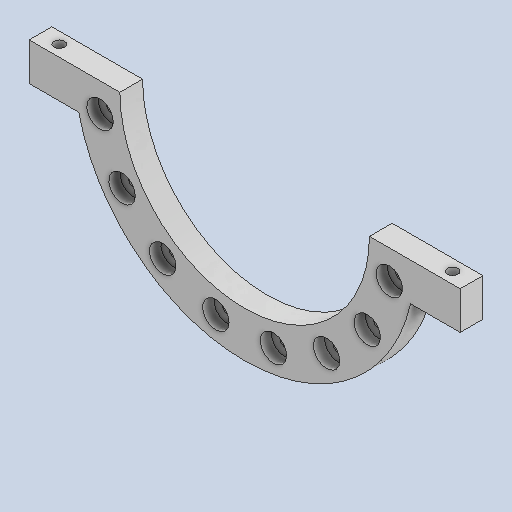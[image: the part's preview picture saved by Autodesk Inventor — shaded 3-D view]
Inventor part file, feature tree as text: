
AUTODESK INVENTOR PART (.ipt)
format: ipt  version: 2025 (Build 290162010, 162A)  size: 263,680 bytes
history: native  units: mm
features: extrude x4, sketch x4, other x2, pattern_circular x1, mirror x1
ambient origin geometry x8: Origin, YZ Plane, XZ Plane, XY Plane, X Axis, Y Axis, Z Axis, Center Point
bodies: Solid1 (feature_tree)
feature tree (12):
  extrude  "Extrusion1"  Depth=30.0mm
  extrude  "Extrusion4"  TaperAngle=0.0deg  [1 undecoded]
  extrude  "Extrusion5"  Depth=15.0mm TaperAngle=0.0deg
  pattern_circular  "Circular Pattern3"  Count=8  [1 undecoded]
  extrude  "Extrusion7"  Depth=50.0mm
  mirror  "Mirror1"
  other  "A-Side Definition"
  sketch  "Sketch1"  dims[d2=30.0mm d3=0.0mm d13=390.0mm]
  sketch  "Sketch4"  dims[d17=13.0mm d18=0.0mm d19=0.0mm]
  sketch  "Sketch5"  dims[d23=35.0mm d24=15.0mm d25=0.0mm d26=80.0mm]
  sketch  "Sketch7"  dims[d27=195.0mm d35=1.963495mm d36=60.0mm d37=80.0mm d38=157.5deg d40=60.0mm d41=50.0mm d42=14.0mm d43=25.0mm d44=0.0mm d45=0.0mm]
  other  "Definition1"
note: 2 required parameter values undecoded (feature->parameter linkage not recoverable at this tier; creation-order binding heuristic only, values carry confidence <= 0.55)
